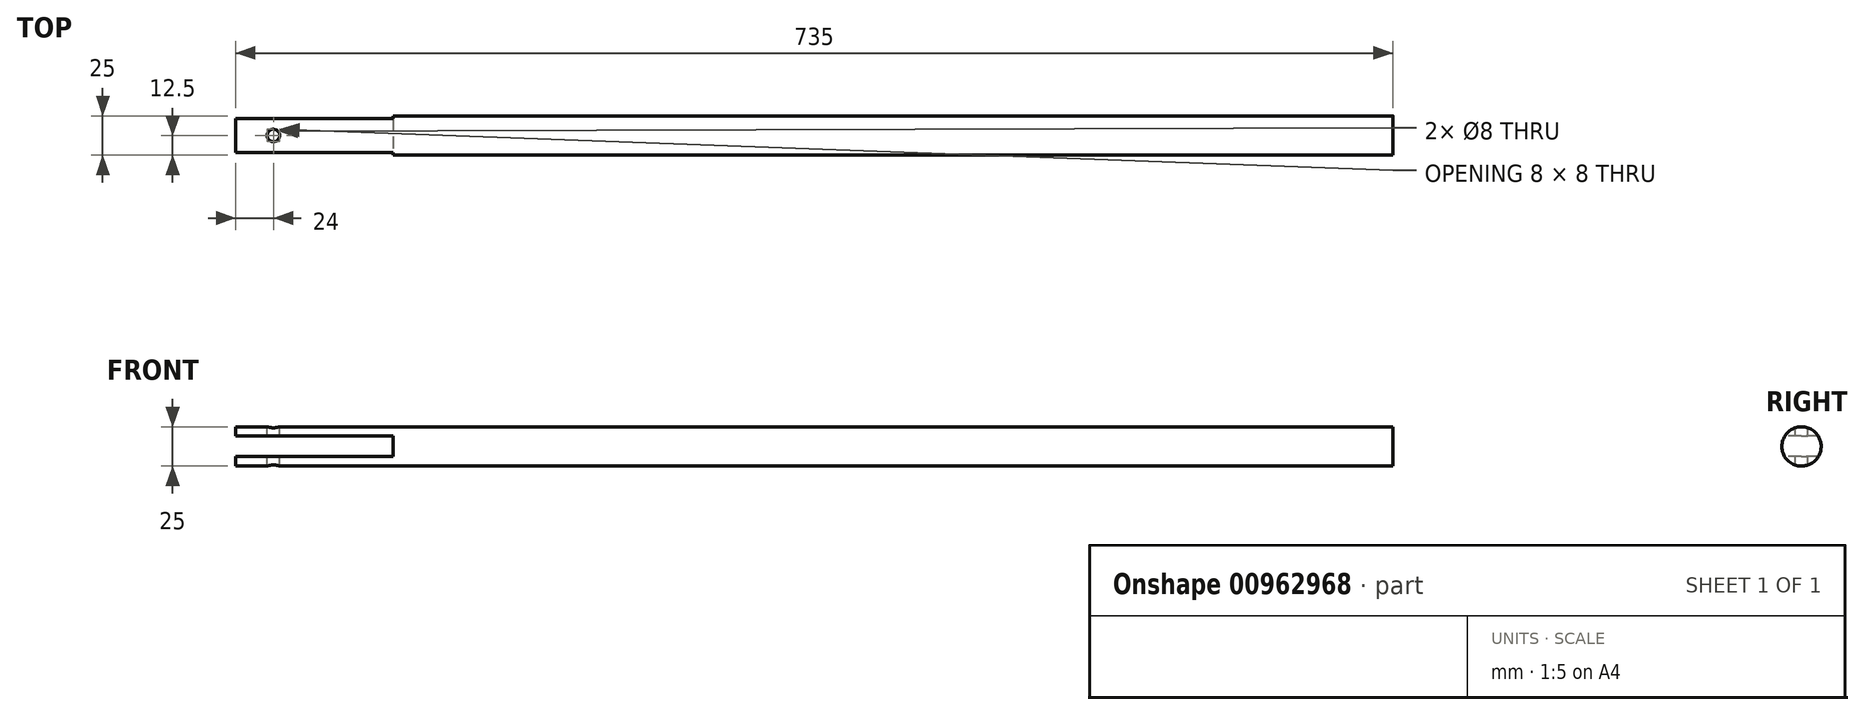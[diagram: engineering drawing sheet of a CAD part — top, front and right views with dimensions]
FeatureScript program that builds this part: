
annotation { "Feature Type Name" : "Feature", "Feature Type Description" : "" }
export const myFeature = defineFeature(function(context is Context, id is Id, definition is map)
    precondition{}
    {
        {
            var Q0;
            Q0=qCreatedBy(makeId("Right.planeOp"),FACE);
            var sketch = newSketch(context, id + "F0", { "sketchPlane" : qUnion([Q0])});
            skCircle(sketch, "E0", {"center": v(0, 0) * mm, "radius": 12.5 * mm});
            skSolve(sketch);
        }
        {
            var Q0;
            Q0=makeQuery(id+"F0.imprint","IMPRINT",FACE,{"disambiguationData":[TD([[makeQuery(id+"F0.imprint","IMPRINT",EDGE,{"derivedFrom":sQuery(id+"F0.wireOp",EDGE,"E0")}),1.0]])]});
            extrude(context, id + "F1", {"entities" : qUnion([Q0]), "depth" : 735 * mm, "offsetDistance" : 25.4 * mm});
        }
        {
            var Q0;
            Q0=qCreatedBy(makeId("Top.planeOp"),FACE);
            var sketch = newSketch(context, id + "F2", { "sketchPlane" : qUnion([Q0])});
            skCircle(sketch, "E1", {"center": v(24, 0) * mm, "radius": 4 * mm});
            skSolve(sketch);
        }
        {
            var Q0;
            Q0=makeQuery(id+"F2.imprint","IMPRINT",FACE,{"disambiguationData":[TD([[makeQuery(id+"F2.imprint","IMPRINT",EDGE,{"derivedFrom":sQuery(id+"F2.wireOp",EDGE,"E1")}),1.0]])]});
            extrude(context, id + "F3", {"entities" : qUnion([Q0]), "operationType" : NewBodyOperationType.REMOVE, "endBound" : BoundingType.UP_TO_NEXT, "oppositeDirection" : true, "depth" : 25.4 * mm, "offsetDistance" : 25.4 * mm, "hasSecondDirection" : true, "secondDirectionBound" : SecondDirectionBoundingType.UP_TO_NEXT, "secondDirectionOppositeDirection" : false, "secondDirectionDepth" : 25.4 * mm});
        }
        {
            var Q0;
            Q0=qCreatedBy(makeId("Front.planeOp"),FACE);
            var sketch = newSketch(context, id + "F4", { "sketchPlane" : qUnion([Q0])});
            skLineSegment(sketch, "E2.bottom", {"start": v(0, 6.5) * mm, "end": v(100, 6.5) * mm});
            skLineSegment(sketch, "E2.top", {"start": v(0, -6.5) * mm, "end": v(100, -6.5) * mm});
            skLineSegment(sketch, "E2.left", {"start": v(0, 6.5) * mm, "end": v(0, -6.5) * mm});
            skLineSegment(sketch, "E2.right", {"start": v(100, 6.5) * mm, "end": v(100, -6.5) * mm});
            skPoint(sketch, "E2.middle", {"position": v(50, 0) * mm});
            skSolve(sketch);
        }
        {
            var Q0;
            Q0 = qSketchRegion(id + "F4", true);
            extrude(context, id + "F5", {"entities" : qUnion([Q0]), "operationType" : NewBodyOperationType.REMOVE, "oppositeDirection" : true, "depth" : 25.4 * mm, "offsetDistance" : 25.4 * mm, "hasSecondDirection" : true, "secondDirectionOppositeDirection" : false, "secondDirectionDepth" : 25.4 * mm});
        }
    });
